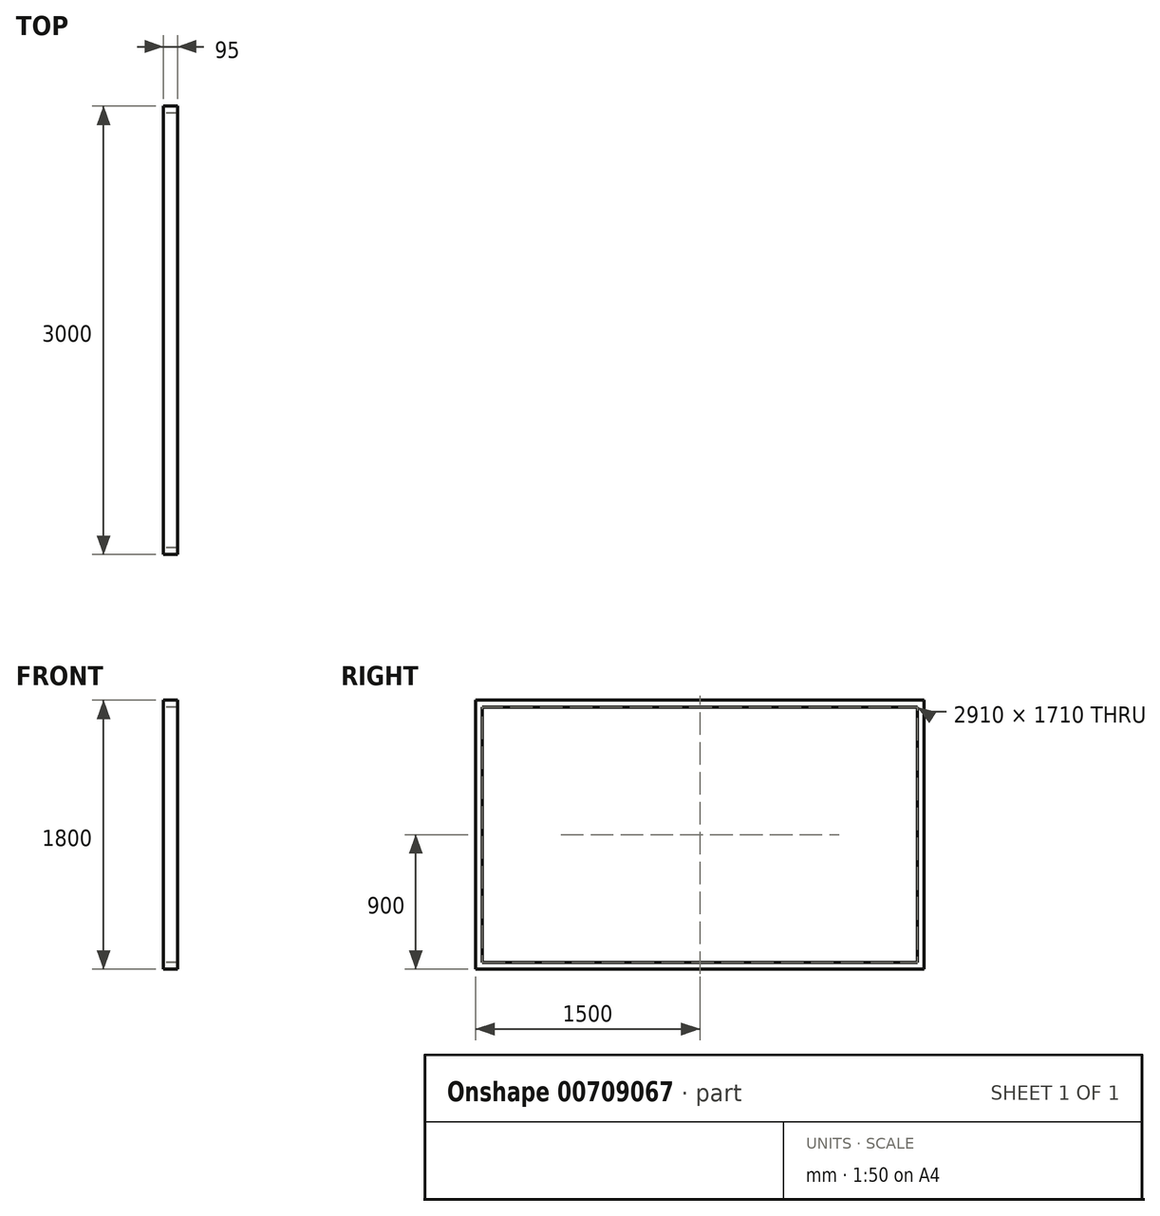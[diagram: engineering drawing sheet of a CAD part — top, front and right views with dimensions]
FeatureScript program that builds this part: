
annotation { "Feature Type Name" : "Feature", "Feature Type Description" : "" }
export const myFeature = defineFeature(function(context is Context, id is Id, definition is map)
    precondition{}
    {
        {
            var Q0;
            Q0=qCreatedBy(makeId("Right.planeOp"),FACE);
            var sketch = newSketch(context, id + "F0", { "sketchPlane" : qUnion([Q0])});
            skLineSegment(sketch, "E0.bottom", {"start": v(-1500, 900) * mm, "end": v(1500, 900) * mm});
            skLineSegment(sketch, "E0.top", {"start": v(-1500, -900) * mm, "end": v(1500, -900) * mm});
            skLineSegment(sketch, "E0.left", {"start": v(-1500, 900) * mm, "end": v(-1500, -900) * mm});
            skLineSegment(sketch, "E0.right", {"start": v(1500, 900) * mm, "end": v(1500, -900) * mm});
            skPoint(sketch, "E0.middle", {"position": v(0, 0) * mm});
            skLineSegment(sketch, "E1", {"start": v(-1500, 855) * mm, "end": v(1500, 855) * mm});
            skLineSegment(sketch, "E2", {"start": v(-1500, -855) * mm, "end": v(1500, -855) * mm});
            skLineSegment(sketch, "E3", {"start": v(1455, 855) * mm, "end": v(1455, -855) * mm});
            skLineSegment(sketch, "E4", {"start": v(-1455, 855) * mm, "end": v(-1455, -855) * mm});
            skLineSegment(sketch, "E5.bottom", {"start": v(-117.5, 855) * mm, "end": v(22.5, 855) * mm});
            skLineSegment(sketch, "E5.top", {"start": v(-22.5, -855) * mm, "end": v(117.5, -855) * mm});
            skLineSegment(sketch, "E6.left", {"start": v(22.5, 22.5) * mm, "end": v(22.5, -22.5) * mm});
            skLineSegment(sketch, "E6.right", {"start": v(1455, 22.5) * mm, "end": v(1455, -22.5) * mm});
            skLineSegment(sketch, "E7.bottom", {"start": v(-1455, 455) * mm, "end": v(1455, 455) * mm});
            skLineSegment(sketch, "E7.top", {"start": v(-1455, 410) * mm, "end": v(1455, 410) * mm});
            skLineSegment(sketch, "E7.left", {"start": v(-1455, 455) * mm, "end": v(-1455, 410) * mm});
            skLineSegment(sketch, "E7.right", {"start": v(1455, 455) * mm, "end": v(1455, 410) * mm});
            skLineSegment(sketch, "E8.bottom", {"start": v(-395, 855) * mm, "end": v(-350, 855) * mm});
            skLineSegment(sketch, "E8.top", {"start": v(-395, 455) * mm, "end": v(-350, 455) * mm});
            skLineSegment(sketch, "E8.left", {"start": v(-395, 855) * mm, "end": v(-395, 455) * mm});
            skLineSegment(sketch, "E8.right", {"start": v(-350, 855) * mm, "end": v(-350, 455) * mm});
            skLineSegment(sketch, "E9.bottom", {"start": v(395, 855) * mm, "end": v(350, 855) * mm});
            skLineSegment(sketch, "E9.top", {"start": v(395, 455) * mm, "end": v(350, 455) * mm});
            skLineSegment(sketch, "E9.left", {"start": v(395, 855) * mm, "end": v(395, 455) * mm});
            skLineSegment(sketch, "E9.right", {"start": v(350, 855) * mm, "end": v(350, 455) * mm});
            skLineSegment(sketch, "E10.bottom", {"start": v(22.5, -855) * mm, "end": v(-22.5, -855) * mm});
            skLineSegment(sketch, "E10.top", {"start": v(22.5, 410) * mm, "end": v(-22.5, 410) * mm});
            skLineSegment(sketch, "E10.left", {"start": v(22.5, -855) * mm, "end": v(22.5, 410) * mm});
            skLineSegment(sketch, "E10.right", {"start": v(-22.5, -855) * mm, "end": v(-22.5, 410) * mm});
            skSolve(sketch);
        }
        {
            var Q0;
            Q0=qSketchRegion(id+"F0",true);
            var Q1;
            {var subQ0=sQuery(id+"F0.wireOp",EDGE,"4hBBfuU4-0Kv4-kc7g-9Pos-s3v09JaGZwlB");Q1=makeQuery(id+"F0.imprint","IMPRINT",FACE,{"disambiguationData":[TD([[makeQuery(id+"F0.imprint","IMPRINT",EDGE,{"derivedFrom":subQ0}),-1.0]])]});}
            var Q2;
            Q2=makeQuery(id+"F0.imprint","IMPRINT",FACE,{"disambiguationData":[TD([[makeQuery(id+"F0.imprint","IMPRINT",EDGE,{"derivedFrom":sQuery(id+"F0.wireOp",EDGE,"E6.bottom")}),-1.0]])]});
            var Q3;
            Q3=makeQuery(id+"F0.imprint","IMPRINT",FACE,{"disambiguationData":[TD([[makeQuery(id+"F0.imprint","IMPRINT",EDGE,{"derivedFrom":sQuery(id+"F0.wireOp",EDGE,"E9.bottom")}),1.0]])]});
            var Q4;
            Q4=makeQuery(id+"F0.imprint","IMPRINT",FACE,{"disambiguationData":[TD([[makeQuery(id+"F0.imprint","IMPRINT",EDGE,{"derivedFrom":sQuery(id+"F0.wireOp",EDGE,"E8.bottom")}),-1.0]])]});
            var Q5;
            {var subQ0=sQuery(id+"F0.wireOp",EDGE,"E7.left");Q5=makeQuery(id+"F0.imprint","IMPRINT",FACE,{"disambiguationData":[TD([[makeQuery(id+"F0.imprint","IMPRINT",EDGE,{"derivedFrom":subQ0}),1.0]])]});}
            var Q6;
            {var subQ3=sQuery(id+"F0.wireOp",EDGE,"E10.bottom");Q6=makeQuery(id+"F0.imprint","IMPRINT",FACE,{"disambiguationData":[TD([[makeQuery(id+"F0.imprint","IMPRINT",EDGE,{"derivedFrom":subQ3}),-1.0]])]});}
            extrude(context, id + "F1", {"entities" : qUnion([Q0, Q1, Q2, Q3, Q4, Q5, Q6]), "depth" : 95 * mm, "offsetDistance" : 25 * mm});
        }
    });
